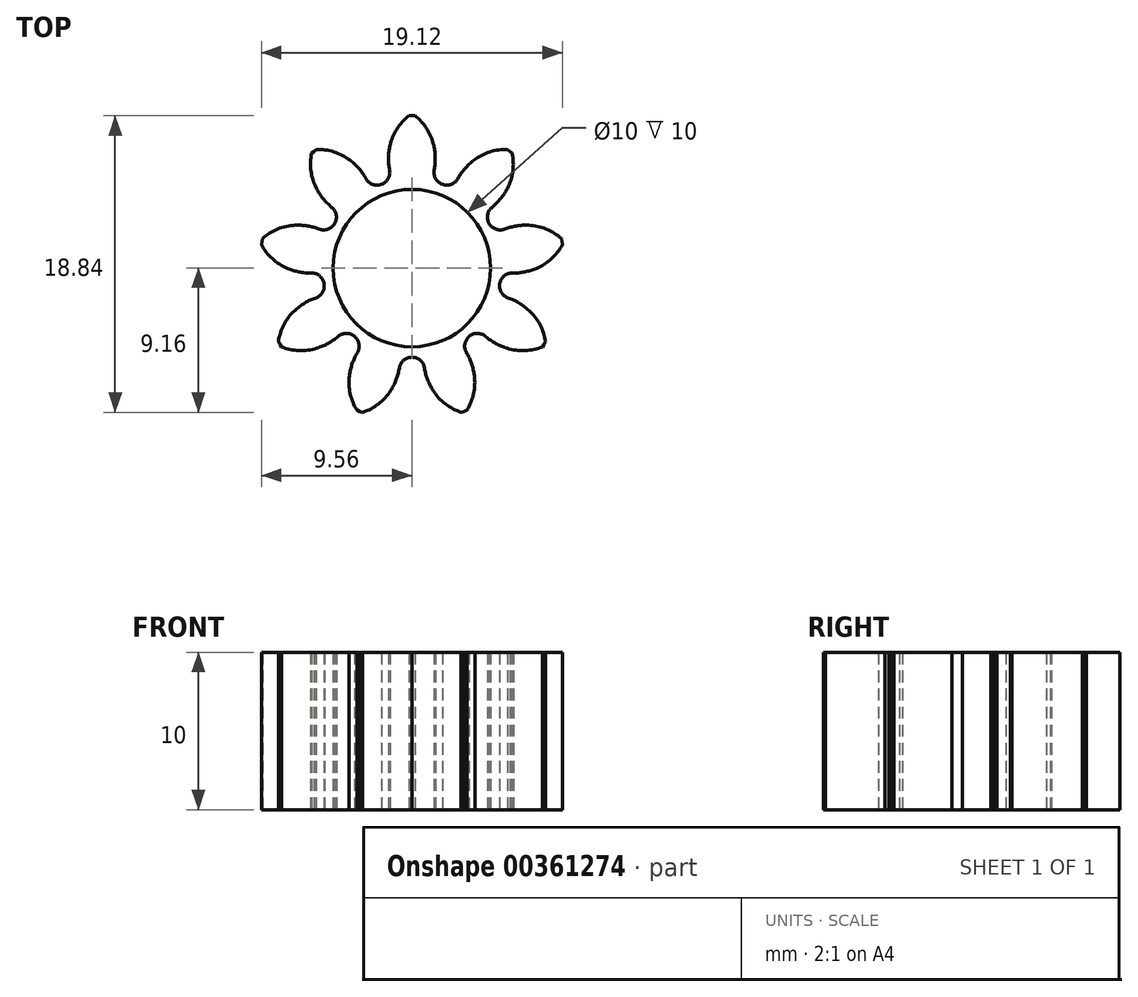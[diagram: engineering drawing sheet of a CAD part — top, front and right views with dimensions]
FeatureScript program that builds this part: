
annotation { "Feature Type Name" : "Feature", "Feature Type Description" : "" }
export const myFeature = defineFeature(function(context is Context, id is Id, definition is map)
    precondition{}
    {
        {
            var Q0;
            Q0=qCreatedBy(makeId("Top.planeOp"),FACE);
            var sketch = newSketch(context, id + "F0", { "sketchPlane" : qUnion([Q0])});
            skCircle(sketch, "E0", {"center": v(0, 0) * mm, "radius": 7.9 * mm, "construction": true});
            skCircle(sketch, "E1", {"center": v(0, 0) * mm, "radius": 9.68 * mm, "construction": true});
            skCircle(sketch, "E2", {"center": v(0, 0) * mm, "radius": 5.68 * mm, "construction": true});
            skLineSegment(sketch, "E3", {"start": v(0, 0) * mm, "end": v(0, 14.6) * mm, "construction": true});
            skLineSegment(sketch, "E4", {"start": v(0, 0) * mm, "end": v(-6.05, 14.6) * mm, "construction": true});
            skLineSegment(sketch, "E5", {"start": v(0, 0) * mm, "end": v(6.05, 14.6) * mm, "construction": true});
            skCircle(sketch, "E6", {"center": v(0, 7.9) * mm, "radius": 1.4 * mm, "construction": true});
            skCircle(sketch, "E7", {"center": v(0, 0) * mm, "radius": 7.3 * mm, "construction": true});
            skCircle(sketch, "E8", {"center": v(1.39, 7.78) * mm, "radius": 3.3 * mm, "construction": true});
            skCircle(sketch, "E9", {"center": v(0, 0) * mm, "radius": 5 * mm});
            skCircle(sketch, "E10", {"center": v(1.39, 7.78) * mm, "radius": 3.77 * mm, "construction": true});
            skArc(sketch, "E11", {"start": v(1.42, 6.23) * mm, "mid": v(1.48, 7) * mm, "end": v(1.39, 7.78) * mm});
            skArc(sketch, "E12.trimOffspring", {"start": v(1.39, 7.78) * mm, "mid": v(0.96, 8.83) * mm, "end": v(0.19, 9.68) * mm});
            skLineSegment(sketch, "E13", {"start": v(2.17, 5.25) * mm, "end": v(1.96, 5.31) * mm});
            skLineSegment(sketch, "E14", {"start": v(0, 9.68) * mm, "end": v(0.19, 9.68) * mm});
            skPoint(sketch, "E15.visualSharp", {"position": v(1.22, 5.55) * mm});
            skArc(sketch, "E15.filletArc", {"start": v(1.42, 6.23) * mm, "mid": v(1.52, 5.67) * mm, "end": v(1.96, 5.31) * mm});
            skLineSegment(sketch, "E16.MirrorCS", {"start": v(-2.17, 5.25) * mm, "end": v(-1.96, 5.31) * mm});
            skLineSegment(sketch, "E17.MirrorCS", {"start": v(0, 9.68) * mm, "end": v(-0.19, 9.68) * mm});
            skArc(sketch, "E18.MirrorCS", {"start": v(-1.39, 7.78) * mm, "mid": v(-0.96, 8.83) * mm, "end": v(-0.19, 9.68) * mm});
            skArc(sketch, "E19.MirrorCS", {"start": v(-1.42, 6.23) * mm, "mid": v(-1.48, 7) * mm, "end": v(-1.39, 7.78) * mm});
            skArc(sketch, "E20.MirrorCS", {"start": v(-1.42, 6.23) * mm, "mid": v(-1.52, 5.67) * mm, "end": v(-1.96, 5.31) * mm});
            skLineSegment(sketch, "E21.1.0", {"start": v(-5.04, 2.62) * mm, "end": v(-4.92, 2.8) * mm});
            skArc(sketch, "E21.1.1", {"start": v(-5.09, 3.86) * mm, "mid": v(-4.8, 3.37) * mm, "end": v(-4.92, 2.8) * mm});
            skArc(sketch, "E21.1.2", {"start": v(-5.09, 3.86) * mm, "mid": v(-5.64, 4.41) * mm, "end": v(-6.06, 5.06) * mm});
            skArc(sketch, "E21.1.3", {"start": v(-6.06, 5.06) * mm, "mid": v(-6.4, 6.15) * mm, "end": v(-6.37, 7.3) * mm});
            skLineSegment(sketch, "E21.1.4", {"start": v(-6.22, 7.42) * mm, "end": v(-6.37, 7.3) * mm});
            skLineSegment(sketch, "E21.1.5", {"start": v(-6.22, 7.42) * mm, "end": v(-6.08, 7.54) * mm});
            skArc(sketch, "E21.1.6", {"start": v(-3.93, 6.85) * mm, "mid": v(-4.95, 7.38) * mm, "end": v(-6.08, 7.54) * mm});
            skArc(sketch, "E21.1.7", {"start": v(-2.92, 5.68) * mm, "mid": v(-3.37, 6.32) * mm, "end": v(-3.93, 6.85) * mm});
            skArc(sketch, "E21.1.8", {"start": v(-2.92, 5.68) * mm, "mid": v(-2.48, 5.32) * mm, "end": v(-1.91, 5.33) * mm});
            skLineSegment(sketch, "E21.1.9", {"start": v(-1.7, 5.42) * mm, "end": v(-1.91, 5.33) * mm});
            skLineSegment(sketch, "E21.2.0", {"start": v(-5.55, -1.23) * mm, "end": v(-5.57, -1.01) * mm});
            skArc(sketch, "E21.2.1", {"start": v(-6.38, -0.31) * mm, "mid": v(-5.84, -0.5) * mm, "end": v(-5.57, -1.01) * mm});
            skArc(sketch, "E21.2.2", {"start": v(-6.38, -0.31) * mm, "mid": v(-7.15, -0.25) * mm, "end": v(-7.9, -0.02) * mm});
            skArc(sketch, "E21.2.3", {"start": v(-7.9, -0.02) * mm, "mid": v(-8.86, 0.6) * mm, "end": v(-9.56, 1.5) * mm});
            skLineSegment(sketch, "E21.2.4", {"start": v(-9.53, 1.68) * mm, "end": v(-9.56, 1.5) * mm});
            skLineSegment(sketch, "E21.2.5", {"start": v(-9.53, 1.68) * mm, "end": v(-9.5, 1.87) * mm});
            skArc(sketch, "E21.2.6", {"start": v(-7.42, 2.72) * mm, "mid": v(-8.53, 2.48) * mm, "end": v(-9.5, 1.87) * mm});
            skArc(sketch, "E21.2.7", {"start": v(-5.89, 2.48) * mm, "mid": v(-6.64, 2.68) * mm, "end": v(-7.42, 2.72) * mm});
            skArc(sketch, "E21.2.8", {"start": v(-5.89, 2.48) * mm, "mid": v(-5.32, 2.48) * mm, "end": v(-4.9, 2.86) * mm});
            skLineSegment(sketch, "E21.2.9", {"start": v(-4.8, 3.05) * mm, "end": v(-4.9, 2.86) * mm});
            skLineSegment(sketch, "E21.3.0", {"start": v(-3.46, -4.5) * mm, "end": v(-3.62, -4.36) * mm});
            skArc(sketch, "E21.3.1", {"start": v(-4.68, -4.34) * mm, "mid": v(-4.15, -4.15) * mm, "end": v(-3.62, -4.36) * mm});
            skArc(sketch, "E21.3.2", {"start": v(-4.68, -4.34) * mm, "mid": v(-5.32, -4.79) * mm, "end": v(-6.04, -5.1) * mm});
            skArc(sketch, "E21.3.3", {"start": v(-6.04, -5.1) * mm, "mid": v(-7.17, -5.24) * mm, "end": v(-8.29, -5) * mm});
            skLineSegment(sketch, "E21.3.4", {"start": v(-8.38, -4.84) * mm, "end": v(-8.29, -5) * mm});
            skLineSegment(sketch, "E21.3.5", {"start": v(-8.38, -4.84) * mm, "end": v(-8.48, -4.68) * mm});
            skArc(sketch, "E21.3.6", {"start": v(-7.43, -2.69) * mm, "mid": v(-8.13, -3.59) * mm, "end": v(-8.48, -4.68) * mm});
            skArc(sketch, "E21.3.7", {"start": v(-6.1, -1.89) * mm, "mid": v(-6.8, -2.22) * mm, "end": v(-7.43, -2.69) * mm});
            skArc(sketch, "E21.3.8", {"start": v(-6.1, -1.89) * mm, "mid": v(-5.67, -1.52) * mm, "end": v(-5.58, -0.96) * mm});
            skLineSegment(sketch, "E21.3.9", {"start": v(-5.63, -0.74) * mm, "end": v(-5.58, -0.96) * mm});
            skLineSegment(sketch, "E21.4.0", {"start": v(0.25, -5.67) * mm, "end": v(0.03, -5.66) * mm});
            skArc(sketch, "E21.4.1", {"start": v(-0.8, -6.34) * mm, "mid": v(-0.51, -5.84) * mm, "end": v(0.03, -5.66) * mm});
            skArc(sketch, "E21.4.2", {"start": v(-0.8, -6.34) * mm, "mid": v(-1, -7.09) * mm, "end": v(-1.35, -7.78) * mm});
            skArc(sketch, "E21.4.3", {"start": v(-1.35, -7.78) * mm, "mid": v(-2.12, -8.63) * mm, "end": v(-3.13, -9.16) * mm});
            skLineSegment(sketch, "E21.4.4", {"start": v(-3.31, -9.1) * mm, "end": v(-3.13, -9.16) * mm});
            skLineSegment(sketch, "E21.4.5", {"start": v(-3.31, -9.1) * mm, "end": v(-3.49, -9.03) * mm});
            skArc(sketch, "E21.4.6", {"start": v(-3.97, -6.83) * mm, "mid": v(-3.92, -7.97) * mm, "end": v(-3.49, -9.03) * mm});
            skArc(sketch, "E21.4.7", {"start": v(-3.46, -5.37) * mm, "mid": v(-3.79, -6.07) * mm, "end": v(-3.97, -6.83) * mm});
            skArc(sketch, "E21.4.8", {"start": v(-3.46, -5.37) * mm, "mid": v(-3.36, -4.8) * mm, "end": v(-3.66, -4.32) * mm});
            skLineSegment(sketch, "E21.4.9", {"start": v(-3.84, -4.19) * mm, "end": v(-3.66, -4.32) * mm});
            skLineSegment(sketch, "E21.5.0", {"start": v(3.84, -4.19) * mm, "end": v(3.66, -4.32) * mm});
            skArc(sketch, "E21.5.1", {"start": v(3.46, -5.37) * mm, "mid": v(3.36, -4.8) * mm, "end": v(3.66, -4.32) * mm});
            skArc(sketch, "E21.5.2", {"start": v(3.46, -5.37) * mm, "mid": v(3.79, -6.07) * mm, "end": v(3.97, -6.83) * mm});
            skArc(sketch, "E21.5.3", {"start": v(3.97, -6.83) * mm, "mid": v(3.92, -7.97) * mm, "end": v(3.49, -9.03) * mm});
            skLineSegment(sketch, "E21.5.4", {"start": v(3.31, -9.1) * mm, "end": v(3.49, -9.03) * mm});
            skLineSegment(sketch, "E21.5.5", {"start": v(3.31, -9.1) * mm, "end": v(3.13, -9.16) * mm});
            skArc(sketch, "E21.5.6", {"start": v(1.35, -7.78) * mm, "mid": v(2.12, -8.63) * mm, "end": v(3.13, -9.16) * mm});
            skArc(sketch, "E21.5.7", {"start": v(0.8, -6.34) * mm, "mid": v(1, -7.09) * mm, "end": v(1.35, -7.78) * mm});
            skArc(sketch, "E21.5.8", {"start": v(0.8, -6.34) * mm, "mid": v(0.51, -5.84) * mm, "end": v(-0.03, -5.66) * mm});
            skLineSegment(sketch, "E21.5.9", {"start": v(-0.25, -5.67) * mm, "end": v(-0.03, -5.66) * mm});
            skLineSegment(sketch, "E21.6.0", {"start": v(5.63, -0.74) * mm, "end": v(5.58, -0.96) * mm});
            skArc(sketch, "E21.6.1", {"start": v(6.1, -1.89) * mm, "mid": v(5.67, -1.52) * mm, "end": v(5.58, -0.96) * mm});
            skArc(sketch, "E21.6.2", {"start": v(6.1, -1.89) * mm, "mid": v(6.8, -2.22) * mm, "end": v(7.43, -2.69) * mm});
            skArc(sketch, "E21.6.3", {"start": v(7.43, -2.69) * mm, "mid": v(8.13, -3.59) * mm, "end": v(8.48, -4.68) * mm});
            skLineSegment(sketch, "E21.6.4", {"start": v(8.38, -4.84) * mm, "end": v(8.48, -4.68) * mm});
            skLineSegment(sketch, "E21.6.5", {"start": v(8.38, -4.84) * mm, "end": v(8.29, -5) * mm});
            skArc(sketch, "E21.6.6", {"start": v(6.04, -5.1) * mm, "mid": v(7.17, -5.24) * mm, "end": v(8.29, -5) * mm});
            skArc(sketch, "E21.6.7", {"start": v(4.68, -4.34) * mm, "mid": v(5.32, -4.79) * mm, "end": v(6.04, -5.1) * mm});
            skArc(sketch, "E21.6.8", {"start": v(4.68, -4.34) * mm, "mid": v(4.15, -4.15) * mm, "end": v(3.62, -4.36) * mm});
            skLineSegment(sketch, "E21.6.9", {"start": v(3.46, -4.5) * mm, "end": v(3.62, -4.36) * mm});
            skLineSegment(sketch, "E21.7.0", {"start": v(4.8, 3.05) * mm, "end": v(4.9, 2.86) * mm});
            skArc(sketch, "E21.7.1", {"start": v(5.89, 2.48) * mm, "mid": v(5.32, 2.48) * mm, "end": v(4.9, 2.86) * mm});
            skArc(sketch, "E21.7.2", {"start": v(5.89, 2.48) * mm, "mid": v(6.64, 2.68) * mm, "end": v(7.42, 2.72) * mm});
            skArc(sketch, "E21.7.3", {"start": v(7.42, 2.72) * mm, "mid": v(8.53, 2.48) * mm, "end": v(9.5, 1.87) * mm});
            skLineSegment(sketch, "E21.7.4", {"start": v(9.53, 1.68) * mm, "end": v(9.5, 1.87) * mm});
            skLineSegment(sketch, "E21.7.5", {"start": v(9.53, 1.68) * mm, "end": v(9.56, 1.5) * mm});
            skArc(sketch, "E21.7.6", {"start": v(7.9, -0.02) * mm, "mid": v(8.86, 0.6) * mm, "end": v(9.56, 1.5) * mm});
            skArc(sketch, "E21.7.7", {"start": v(6.38, -0.31) * mm, "mid": v(7.15, -0.25) * mm, "end": v(7.9, -0.02) * mm});
            skArc(sketch, "E21.7.8", {"start": v(6.38, -0.31) * mm, "mid": v(5.84, -0.5) * mm, "end": v(5.57, -1.01) * mm});
            skLineSegment(sketch, "E21.7.9", {"start": v(5.55, -1.23) * mm, "end": v(5.57, -1.01) * mm});
            skLineSegment(sketch, "E21.8.0", {"start": v(1.7, 5.42) * mm, "end": v(1.91, 5.33) * mm});
            skArc(sketch, "E21.8.1", {"start": v(2.92, 5.68) * mm, "mid": v(2.48, 5.32) * mm, "end": v(1.91, 5.33) * mm});
            skArc(sketch, "E21.8.2", {"start": v(2.92, 5.68) * mm, "mid": v(3.37, 6.32) * mm, "end": v(3.93, 6.85) * mm});
            skArc(sketch, "E21.8.3", {"start": v(3.93, 6.85) * mm, "mid": v(4.95, 7.38) * mm, "end": v(6.08, 7.54) * mm});
            skLineSegment(sketch, "E21.8.4", {"start": v(6.22, 7.42) * mm, "end": v(6.08, 7.54) * mm});
            skLineSegment(sketch, "E21.8.5", {"start": v(6.22, 7.42) * mm, "end": v(6.37, 7.3) * mm});
            skArc(sketch, "E21.8.6", {"start": v(6.06, 5.06) * mm, "mid": v(6.4, 6.15) * mm, "end": v(6.37, 7.3) * mm});
            skArc(sketch, "E21.8.7", {"start": v(5.09, 3.86) * mm, "mid": v(5.64, 4.41) * mm, "end": v(6.06, 5.06) * mm});
            skArc(sketch, "E21.8.8", {"start": v(5.09, 3.86) * mm, "mid": v(4.8, 3.37) * mm, "end": v(4.92, 2.8) * mm});
            skLineSegment(sketch, "E21.8.9", {"start": v(5.04, 2.62) * mm, "end": v(4.92, 2.8) * mm});
            skSolve(sketch);
        }
        {
            var Q0;
            Q0=makeQuery(id+"F0.imprint","IMPRINT",FACE,{"disambiguationData":[TD([[makeQuery(id+"F0.imprint","IMPRINT",EDGE,{"derivedFrom":sQuery(id+"F0.wireOp",EDGE,"E9")}),-1.0]])]});
            extrude(context, id + "F1", {"entities" : qUnion([Q0]), "depth" : 10 * mm});
        }
    });
